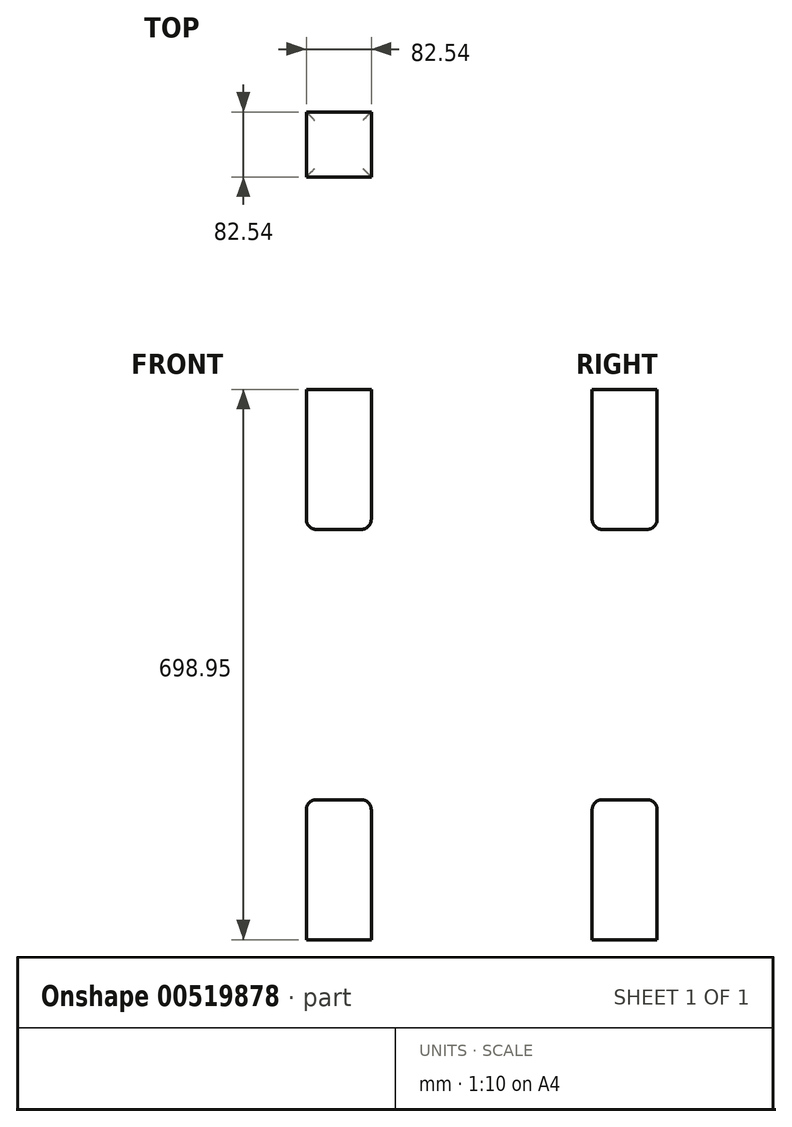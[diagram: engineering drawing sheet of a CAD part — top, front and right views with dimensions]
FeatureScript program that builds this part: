
annotation { "Feature Type Name" : "Feature", "Feature Type Description" : "" }
export const myFeature = defineFeature(function(context is Context, id is Id, definition is map)
    precondition{}
    {
        {
            var Q0;
            Q0=qCreatedBy(makeId("Front.planeOp"),FACE);
            var sketch = newSketch(context, id + "F0", { "sketchPlane" : qUnion([Q0])});
            skPoint(sketch, "E0.middle", {"position": v(0, 0) * mm});
            skLineSegment(sketch, "E1", {"start": v(0, 227.79) * mm, "end": v(0, -115.56) * mm, "construction": true});
            skArc(sketch, "E2", {"start": v(26.31, 182.71) * mm, "mid": v(38.89, 205.25) * mm, "end": v(26.31, 227.79) * mm});
            skArc(sketch, "E3", {"start": v(26.31, 164.74) * mm, "mid": v(32.7, 173.73) * mm, "end": v(26.31, 182.71) * mm});
            skArc(sketch, "E4", {"start": v(26.31, -49.64) * mm, "mid": v(36.4, 57.55) * mm, "end": v(26.31, 164.74) * mm});
            skArc(sketch, "E5", {"start": v(26.31, -67.63) * mm, "mid": v(32.73, -58.64) * mm, "end": v(26.31, -49.64) * mm});
            skArc(sketch, "E6", {"start": v(26.31, -115.56) * mm, "mid": v(35.83, -91.6) * mm, "end": v(26.31, -67.63) * mm});
            skPoint(sketch, "E0.top.end.orphan", {"position": v(-44.45, 447.68) * mm});
            skPoint(sketch, "E0.left.end.orphan", {"position": v(44.45, 447.68) * mm});
            skPoint(sketch, "E7.orphan", {"position": v(44.45, -447.68) * mm});
            skPoint(sketch, "E0.bottom.end.orphan", {"position": v(-44.45, -447.68) * mm});
            skPoint(sketch, "E8.end.orphan", {"position": v(0, -115.56) * mm});
            skLineSegment(sketch, "E9", {"start": v(26.31, 227.79) * mm, "end": v(0, 227.79) * mm});
            skLineSegment(sketch, "E10", {"start": v(26.31, -115.56) * mm, "end": v(0, -115.56) * mm});
            skPoint(sketch, "E11.orphan", {"position": v(0, -447.68) * mm});
            skPoint(sketch, "E12.orphan", {"position": v(0, 447.68) * mm});
            skSolve(sketch);
        }
        {
            var Q0;
            Q0=sQuery(id+"F0.wireOp",EDGE,"E9");
            var Q1;
            Q1=sQuery(id+"F0.wireOp",EDGE,"E2");
            var Q2;
            Q2=sQuery(id+"F0.wireOp",EDGE,"E3");
            var Q3;
            Q3=sQuery(id+"F0.wireOp",EDGE,"E4");
            var Q4;
            Q4=sQuery(id+"F0.wireOp",EDGE,"E5");
            var Q5;
            Q5=sQuery(id+"F0.wireOp",EDGE,"E6");
            var Q6;
            Q6=sQuery(id+"F0.wireOp",EDGE,"E10");
            var Q7;
            Q7=sQuery(id+"F0.wireOp",EDGE,"E1");
            revolve(context, id + "F1", {"bodyType" : ToolBodyType.SURFACE, "surfaceEntities" : qUnion([Q0, Q1, Q2, Q3, Q4, Q5, Q6]), "axis" : qUnion([Q7]), "revolveType" : RevolveType.FULL});
        }
        {
            var Q0;
            Q0=makeQuery(id+"F1.opRevolve","SWEPT_FACE",FACE,{"disambiguationData":[OSD([sQuery(id+"F0.wireOp",EDGE,"E9")])]});
            var sketch = newSketch(context, id + "F2", { "sketchPlane" : qUnion([Q0])});
            skLineSegment(sketch, "E13.bottom", {"start": v(41.28, -41.27) * mm, "end": v(-41.28, -41.28) * mm});
            skLineSegment(sketch, "E13.top", {"start": v(41.27, 41.28) * mm, "end": v(-41.28, 41.28) * mm});
            skLineSegment(sketch, "E13.left", {"start": v(41.28, -41.27) * mm, "end": v(41.27, 41.28) * mm});
            skLineSegment(sketch, "E13.right", {"start": v(-41.28, -41.28) * mm, "end": v(-41.28, 41.28) * mm});
            skPoint(sketch, "E13.middle", {"position": v(0, 0) * mm});
            skSolve(sketch);
        }
        {
            var Q0;
            Q0 = qSketchRegion(id + "F2", true);
            extrude(context, id + "F3", {"entities" : qUnion([Q0]), "depth" : 177.8 * mm, "offsetDistance" : 25.4 * mm});
        }
        {
            var Q0;
            Q0=makeQuery(id+"F1.opRevolve","SWEPT_FACE",FACE,{"disambiguationData":[OSD([sQuery(id+"F0.wireOp",EDGE,"E10")])]});
            var sketch = newSketch(context, id + "F4", { "sketchPlane" : qUnion([Q0])});
            skLineSegment(sketch, "E14.bottom", {"start": v(41.28, -41.27) * mm, "end": v(-41.27, -41.28) * mm});
            skLineSegment(sketch, "E14.top", {"start": v(41.27, 41.28) * mm, "end": v(-41.28, 41.28) * mm});
            skLineSegment(sketch, "E14.left", {"start": v(41.28, -41.27) * mm, "end": v(41.27, 41.28) * mm});
            skLineSegment(sketch, "E14.right", {"start": v(-41.27, -41.28) * mm, "end": v(-41.28, 41.28) * mm});
            skPoint(sketch, "E14.middle", {"position": v(0, 0) * mm});
            skSolve(sketch);
        }
        {
            var Q0;
            Q0 = qSketchRegion(id + "F4", true);
            extrude(context, id + "F5", {"entities" : qUnion([Q0]), "depth" : 177.8 * mm, "offsetDistance" : 25.4 * mm});
        }
        {
            var Q0;
            Q0=makeQuery(id+"F5.opExtrude","CAP_FACE",FACE,{"disambiguationData":[OSD([sQuery(id+"F4.wireOp",EDGE,"E14.bottom"),sQuery(id+"F4.wireOp",EDGE,"E14.top"),sQuery(id+"F4.wireOp",EDGE,"E14.left"),sQuery(id+"F4.wireOp",EDGE,"E14.right")])],"isStart":true});
            fillet(context, id + "F6", {"entities" : qUnion([Q0]), "radius" : 12.7 * mm, "tangentPropagation" : true, "allowEdgeOverflow" : false});
        }
        {
            var Q0;
            Q0=makeQuery(id+"F3.opExtrude","CAP_FACE",FACE,{"disambiguationData":[OSD([sQuery(id+"F2.wireOp",EDGE,"E13.bottom"),sQuery(id+"F2.wireOp",EDGE,"E13.top"),sQuery(id+"F2.wireOp",EDGE,"E13.left"),sQuery(id+"F2.wireOp",EDGE,"E13.right")])],"isStart":true});
            fillet(context, id + "F7", {"entities" : qUnion([Q0]), "radius" : 12.7 * mm, "tangentPropagation" : true, "allowEdgeOverflow" : false});
        }
    });
